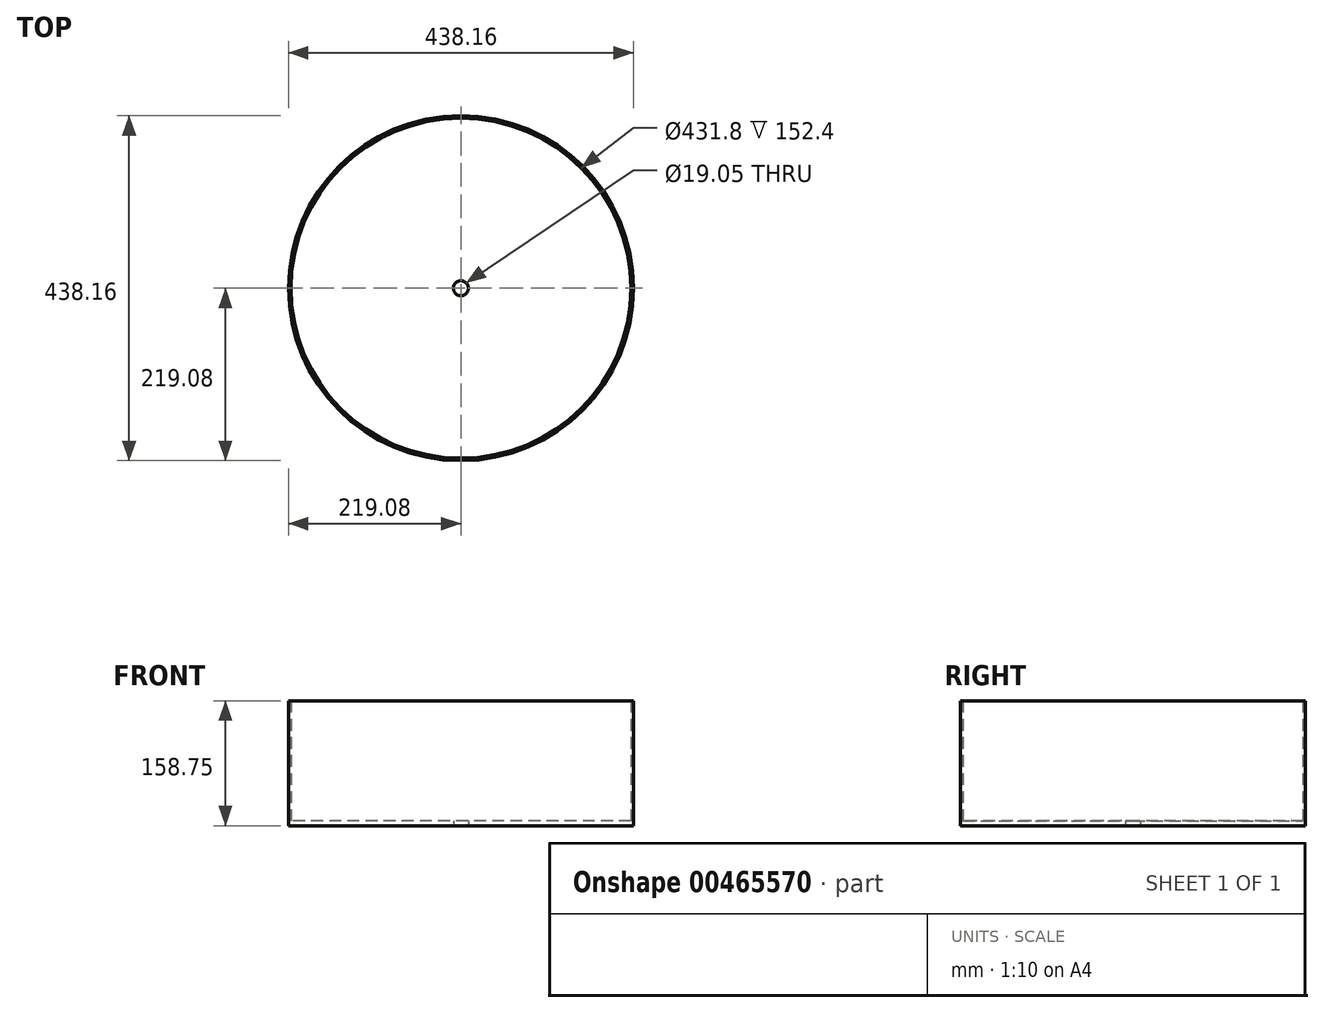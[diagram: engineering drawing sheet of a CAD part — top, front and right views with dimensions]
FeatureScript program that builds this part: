
annotation { "Feature Type Name" : "Feature", "Feature Type Description" : "" }
export const myFeature = defineFeature(function(context is Context, id is Id, definition is map)
    precondition{}
    {
        {
            var Q0;
            Q0=qCreatedBy(makeId("Top.planeOp"),FACE);
            var sketch = newSketch(context, id + "F0", { "sketchPlane" : qUnion([Q0])});
            skCircle(sketch, "E0", {"center": v(0, 0) * mm, "radius": 215.9 * mm});
            skCircle(sketch, "E1", {"center": v(0, 0) * mm, "radius": 219.08 * mm});
            skSolve(sketch);
        }
        {
            var Q0;
            Q0=makeQuery(id+"F0.imprint","IMPRINT",FACE,{"disambiguationData":[TD([[makeQuery(id+"F0.imprint","IMPRINT",EDGE,{"derivedFrom":sQuery(id+"F0.wireOp",EDGE,"E0")}),-1.0]])]});
            extrude(context, id + "F1", {"entities" : qUnion([Q0]), "depth" : 152.4 * mm});
        }
        {
            var Q0;
            Q0=qCreatedBy(makeId("Top.planeOp"),FACE);
            var sketch = newSketch(context, id + "F2", { "sketchPlane" : qUnion([Q0])});
            skCircle(sketch, "E2", {"center": v(0, 0) * mm, "radius": 219.08 * mm});
            skSolve(sketch);
        }
        {
            var Q0;
            Q0 = qSketchRegion(id + "F2", true);
            extrude(context, id + "F3", {"entities" : qUnion([Q0]), "operationType" : NewBodyOperationType.ADD, "oppositeDirection" : true, "depth" : 6.35 * mm});
        }
        {
            var Q0;
            Q0=makeQuery(id+"F3.opExtrude","CAP_FACE",FACE,{"disambiguationData":[OSD([sQuery(id+"F2.wireOp",EDGE,"E2")])],"isStart":false});
            var sketch = newSketch(context, id + "F4", { "sketchPlane" : qUnion([Q0])});
            skCircle(sketch, "E3", {"center": v(0, 0) * mm, "radius": 9.53 * mm});
            skSolve(sketch);
        }
        {
            var Q0;
            Q0 = qSketchRegion(id + "F4", true);
            extrude(context, id + "F5", {"entities" : qUnion([Q0]), "operationType" : NewBodyOperationType.REMOVE, "oppositeDirection" : true, "depth" : 25.4 * mm});
        }
    });
